# Revit family: Acoustic_Panels_Stratus_Primacoustic
name_source: partatom
category: Generic Models
units: mm (PartAtom-declared; Revit-internal decimal feet)

## family parameters
Can host rebar = No
Cut with Voids When Loaded = No
Host = Face
Maintain Annotation Orientation = No
Part Type = Normal
Room Calculation Point = No
Round Connector Dimension = Use Diameter
Shared = No

## types (4) — shared parameters
CAD Details = https://www.arcat.com
Datasheet = https://www.primacoustic.com
Description = Stratus Studio Ceiling Cloud
Edge options = Square
Finish = Fabric
Hook Material = Hook
Keynote = 09 80 00
Manufacturer = Primacoustic
Name = Stratus
Panel Core Material = Panel Core
Panel Depth = 24 "
Panel Thickness = 2 "
Panel Width = 48 "
Panels per box = 1
Product Page URL = https://www.arcat.com
Product name = Stratus Studio Ceiling Cloud
Surface Area Coverage = 8 sq-ft (0.7 sq-meters)
This panel is also available in kit form = Yes
URL = https://www.primacoustic.com
zero-valued in all types: Default Elevation

## per-type parameters (varying)
| type | Panel Material | Specification |
| Z840-1200-00 | 00_Black | https://www.arcat.com |
| Z840-1200-03 | 03_Beige | https://www.arcat.com |
| Z840-1200-08 | 08_Gray | https://www.arcat.com |
| Z840-1200-09 | 09_Paintable | https://www.arcat.com
https://www.arcat.com
https://www.arcat.com |

note: column(s) folded — value = type name in every type: Model, Part #

## geometry (parser evidence)
native form markers: Sweep x6
no freeform markers — native parametric forms only
